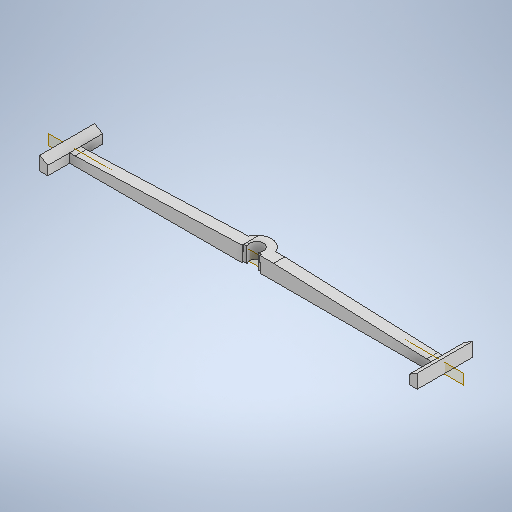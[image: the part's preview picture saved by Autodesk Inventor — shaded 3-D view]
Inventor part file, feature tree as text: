
AUTODESK INVENTOR PART (.ipt)
format: ipt  version: 2025.1 (Build 291241000, 241)  size: 345,088 bytes
history: native  units: mm
features: extrude x6, sketch x6, plane x1
ambient origin geometry x8: Origin, YZ Plane, XZ Plane, XY Plane, X Axis, Y Axis, Z Axis, Center Point
bodies: Volumenkörper1 (feature_tree)
feature tree (13):
  extrude  "Extrusion1"  Depth=2.85mm
  plane  "Arbeitsebene1"
  extrude  "Extrusion2"  Depth=2.85mm
  extrude  "Extrusion3"  Depth=19.7mm
  extrude  "Extrusion4"  Depth=5.5mm TaperAngle=0.0deg
  extrude  "Extrusion5"  Depth=60.0mm
  extrude  "Extrusion6"  Depth=2.25mm
  sketch  "Skizze1"  dims[d0=135.6mm d1=4.0mm d2=3.25mm d3=0.0mm d4=2.85mm]
  sketch  "Skizze2"  dims[d5=1.75mm d6=2.85mm]
  sketch  "Skizze3"  dims[d7=19.7mm d8=0.0mm d9=7.795mm]
  sketch  "Skizze4"  dims[d10=0.0mm d11=0.0mm d15=5.5mm d16=0.0mm]
  sketch  "Skizze5"  dims[d17=60.0mm d18=60.0mm]
  sketch  "Skizze6"  dims[d19=2.25mm d20=0.0mm d21=55.0mm d22=2.25mm d23=55.0mm d24=0.0mm d25=0.0mm d26=2.25mm d27=2.8mm d28=4.99mm d29=1.4mm]
